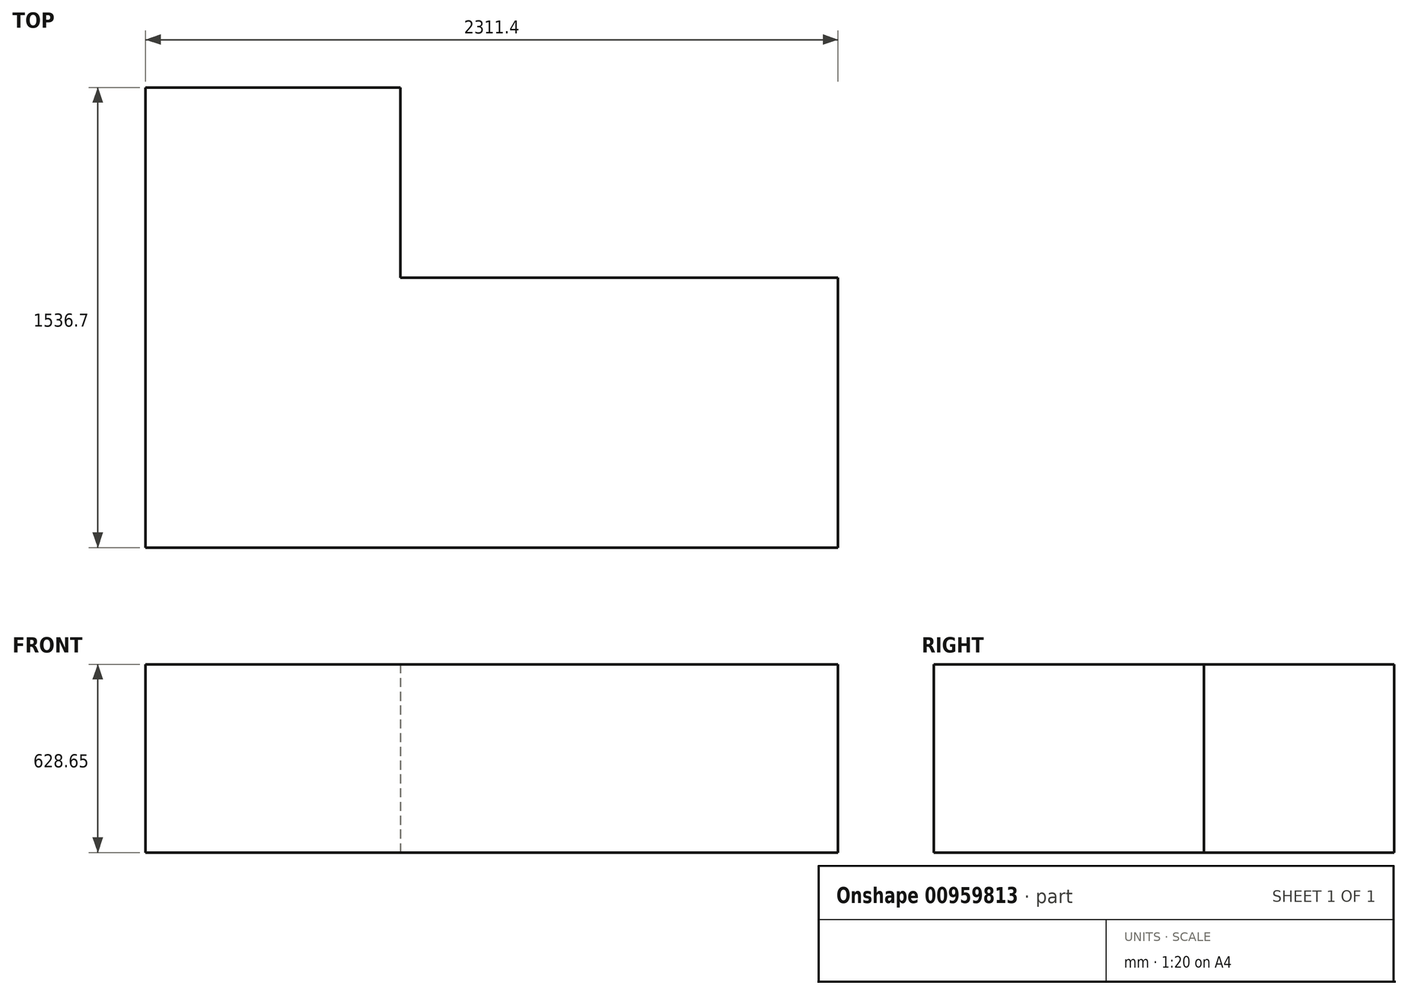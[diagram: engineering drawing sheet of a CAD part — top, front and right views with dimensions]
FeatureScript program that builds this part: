
annotation { "Feature Type Name" : "Feature", "Feature Type Description" : "" }
export const myFeature = defineFeature(function(context is Context, id is Id, definition is map)
    precondition{}
    {
        {
            var Q0;
            Q0=qCreatedBy(makeId("Top.planeOp"),FACE);
            var sketch = newSketch(context, id + "F0", { "sketchPlane" : qUnion([Q0])});
            skLineSegment(sketch, "E0", {"start": v(0, 0) * mm, "end": v(850.9, 0) * mm});
            skLineSegment(sketch, "E1", {"start": v(0, 0) * mm, "end": v(0, -1536.7) * mm});
            skLineSegment(sketch, "E2", {"start": v(0, -1536.7) * mm, "end": v(2311.4, -1536.7) * mm});
            skLineSegment(sketch, "E3", {"start": v(2311.4, -1536.7) * mm, "end": v(2311.4, -635) * mm});
            skLineSegment(sketch, "E4", {"start": v(2311.4, -635) * mm, "end": v(850.9, -635) * mm});
            skLineSegment(sketch, "E5", {"start": v(850.9, -635) * mm, "end": v(850.9, 0) * mm});
            skSolve(sketch);
        }
        {
            var Q0;
            Q0=makeQuery(id+"F0.imprint","IMPRINT",FACE,{"disambiguationData":[TD([[makeQuery(id+"F0.imprint","IMPRINT",EDGE,{"derivedFrom":sQuery(id+"F0.wireOp",EDGE,"E0")}),-1.0]])]});
            extrude(context, id + "F1", {"entities" : qUnion([Q0]), "depth" : 628.65 * mm, "offsetDistance" : 25.4 * mm});
        }
    });
